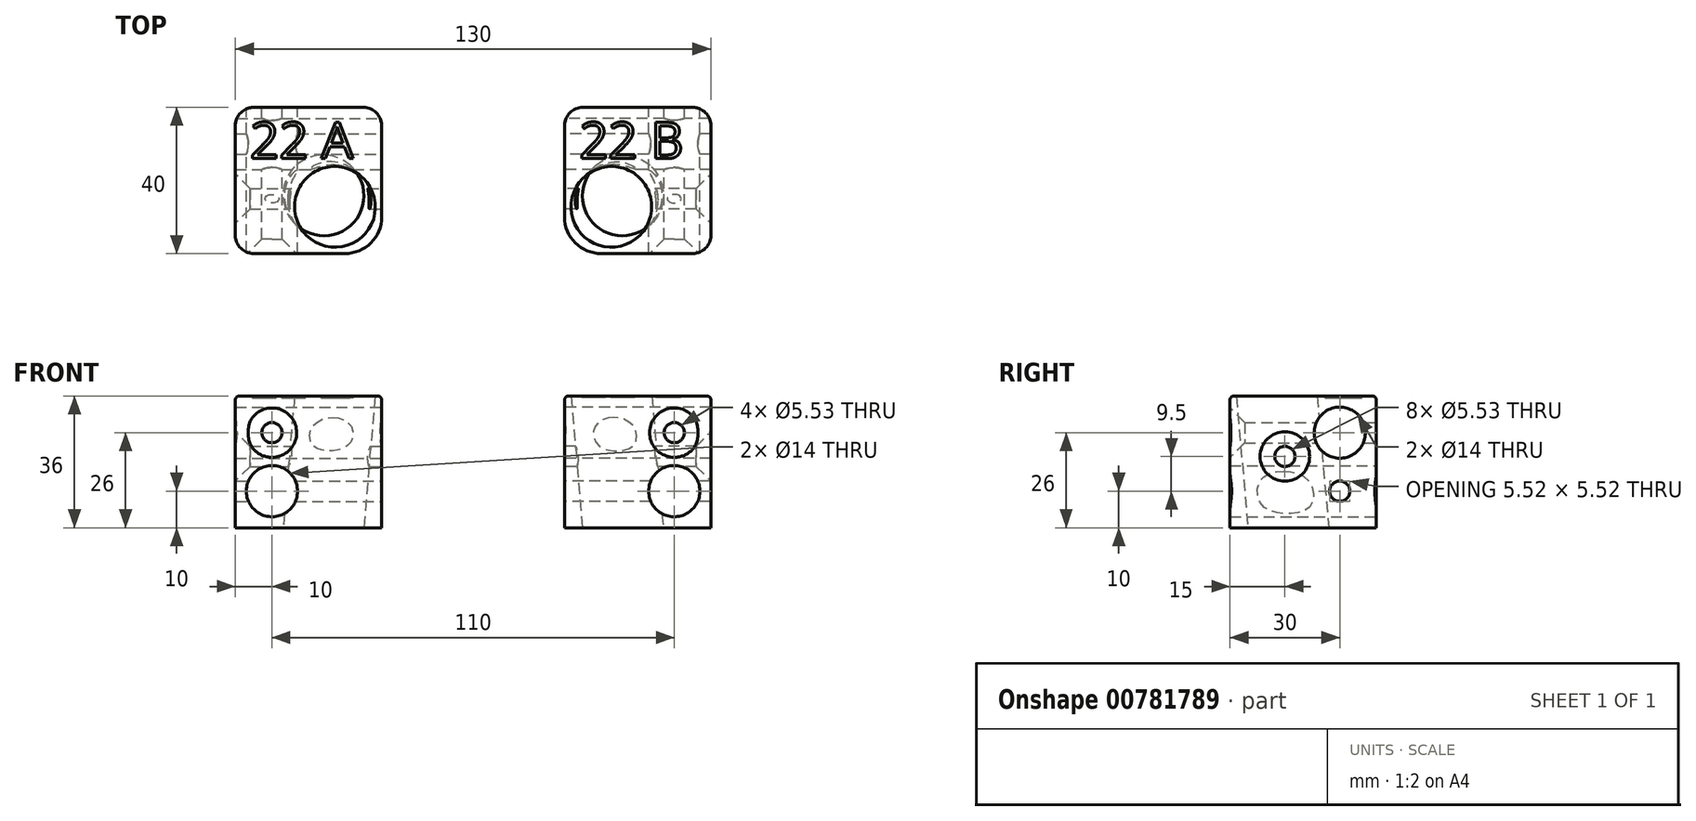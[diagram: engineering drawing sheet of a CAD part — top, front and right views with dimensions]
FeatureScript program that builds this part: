
annotation { "Feature Type Name" : "Feature", "Feature Type Description" : "" }
export const myFeature = defineFeature(function(context is Context, id is Id, definition is map)
    precondition{}
    {
        {
            var Q0;
            Q0=qCreatedBy(makeId("Right.planeOp"),FACE);
            var sketch = newSketch(context, id + "F0", { "sketchPlane" : qUnion([Q0])});
            skLineSegment(sketch, "E0", {"start": v(0, 0) * mm, "end": v(0, 73.22) * mm});
            skSolve(sketch);
        }
        {
            var Q0;
            Q0=sQuery(id+"F0.wireOp",EDGE,"E0");
            var Q1;
            Q1=qCreatedBy(makeId("Right.planeOp"),FACE);
            cPlane(context, id + "F1", {"entities" : qUnion([Q0, Q1]), "cplaneType" : CPlaneType.LINE_ANGLE, "offset" : 25 * mm, "angle" : 45 * degree, "width" : 150 * mm, "height" : 150 * mm});
        }
        {
            var Q0;
            Q0=qCreatedBy(makeId("Top.planeOp"),FACE);
            var sketch = newSketch(context, id + "F2", { "sketchPlane" : qUnion([Q0])});
            skLineSegment(sketch, "E1", {"start": v(0, 0) * mm, "end": v(6.32, 6.32) * mm});
            skSolve(sketch);
        }
        {
            var Q0;
            Q0=sQuery(id+"F2.wireOp",EDGE,"E1");
            var Q1;
            Q1=qCreatedBy(makeId("Top.planeOp"),FACE);
            cPlane(context, id + "F3", {"entities" : qUnion([Q0, Q1]), "cplaneType" : CPlaneType.LINE_ANGLE, "offset" : 25 * mm, "angle" : 7 * degree, "width" : 150 * mm, "height" : 150 * mm});
        }
        {
            var Q0;
            Q0=qCreatedBy(makeId("Top.planeOp"),FACE);
            var sketch = newSketch(context, id + "F4", { "sketchPlane" : qUnion([Q0])});
            skLineSegment(sketch, "E2.bottom", {"start": v(20, -20) * mm, "end": v(-20, -20) * mm});
            skLineSegment(sketch, "E2.top", {"start": v(20, 20) * mm, "end": v(-20, 20) * mm});
            skLineSegment(sketch, "E2.left", {"start": v(20, -20) * mm, "end": v(20, 20) * mm});
            skLineSegment(sketch, "E2.right", {"start": v(-20, -20) * mm, "end": v(-20, 20) * mm});
            skPoint(sketch, "E2.middle", {"position": v(0, 0) * mm});
            skSolve(sketch);
        }
        {
            var Q0;
            Q0=makeQuery(id+"F4.imprint","IMPRINT",FACE,{"disambiguationData":[TD([[makeQuery(id+"F4.imprint","IMPRINT",EDGE,{"derivedFrom":sQuery(id+"F4.wireOp",EDGE,"E2.bottom")}),-1.0]])]});
            extrude(context, id + "F5", {"entities" : qUnion([Q0]), "depth" : 36 * mm, "offsetDistance" : 25 * mm});
        }
        {
            var Q0;
            Q0=qCreatedBy(id+"F3.planeOp",FACE);
            var sketch = newSketch(context, id + "F6", { "sketchPlane" : qUnion([Q0])});
            skCircle(sketch, "E3", {"center": v(4.04, 4.07) * mm, "radius": 11 * mm});
            skSolve(sketch);
        }
        {
            var Q0;
            Q0 = qSketchRegion(id + "F6", true);
            extrude(context, id + "F7", {"entities" : qUnion([Q0]), "operationType" : NewBodyOperationType.REMOVE, "endBound" : BoundingType.SYMMETRIC, "oppositeDirection" : true, "depth" : 150 * mm, "offsetDistance" : 25 * mm});
        }
        {
            var Q0;
            Q0=makeQuery(id+"F5.opExtrude","SWEPT_FACE",FACE,{"disambiguationData":[OSD([sQuery(id+"F4.wireOp",EDGE,"E2.left")])]});
            var sketch = newSketch(context, id + "F8", { "sketchPlane" : qUnion([Q0])});
            skCircle(sketch, "E4", {"center": v(10, 26) * mm, "radius": 7 * mm});
            skCircle(sketch, "E5", {"center": v(10, 10) * mm, "radius": 2.76 * mm});
            skCircle(sketch, "E6", {"center": v(-5, 19.5) * mm, "radius": 2.76 * mm});
            skSolve(sketch);
        }
        {
            var Q0;
            Q0 = qSketchRegion(id + "F8", true);
            extrude(context, id + "F9", {"entities" : qUnion([Q0]), "operationType" : NewBodyOperationType.REMOVE, "endBound" : BoundingType.THROUGH_ALL, "oppositeDirection" : true, "depth" : 25 * mm, "offsetDistance" : 25 * mm});
        }
        {
            var Q0;
            Q0=makeQuery(id+"F5.opExtrude","SWEPT_FACE",FACE,{"disambiguationData":[OSD([sQuery(id+"F4.wireOp",EDGE,"E2.top")])]});
            var sketch = newSketch(context, id + "F10", { "sketchPlane" : qUnion([Q0])});
            skCircle(sketch, "E7", {"center": v(10, 10) * mm, "radius": 7 * mm});
            skCircle(sketch, "E8", {"center": v(10, 26) * mm, "radius": 2.76 * mm});
            skSolve(sketch);
        }
        {
            var Q0;
            Q0 = qSketchRegion(id + "F10", true);
            extrude(context, id + "F11", {"entities" : qUnion([Q0]), "operationType" : NewBodyOperationType.REMOVE, "endBound" : BoundingType.THROUGH_ALL, "oppositeDirection" : true, "depth" : 25 * mm, "offsetDistance" : 25 * mm});
        }
        {
            var Q0;
            Q0=makeQuery(id+"F5.opExtrude","SWEPT_EDGE",EDGE,{"disambiguationData":[OSD([sQuery(id+"F4.wireOp",EDGE,"E2.bottom"),sQuery(id+"F4.wireOp",EDGE,"E2.left")])]});
            fillet(context, id + "F12", {"entities" : qUnion([Q0]), "radius" : 10 * mm, "tangentPropagation" : true, "allowEdgeOverflow" : false});
        }
        {
            var Q0;
            Q0=makeQuery(id+"F5.opExtrude","SWEPT_EDGE",EDGE,{"disambiguationData":[OSD([sQuery(id+"F4.wireOp",EDGE,"E2.bottom"),sQuery(id+"F4.wireOp",EDGE,"E2.right")])]});
            var Q1;
            Q1=makeQuery(id+"F5.opExtrude","SWEPT_EDGE",EDGE,{"disambiguationData":[OSD([sQuery(id+"F4.wireOp",EDGE,"E2.top"),sQuery(id+"F4.wireOp",EDGE,"E2.right")])]});
            var Q2;
            Q2=makeQuery(id+"F5.opExtrude","SWEPT_EDGE",EDGE,{"disambiguationData":[OSD([sQuery(id+"F4.wireOp",EDGE,"E2.top"),sQuery(id+"F4.wireOp",EDGE,"E2.left")])]});
            fillet(context, id + "F13", {"entities" : qUnion([Q0, Q1, Q2]), "radius" : 5 * mm, "tangentPropagation" : true, "allowEdgeOverflow" : false});
        }
        {
            var Q0;
            Q0=makeQuery(id+"F5.opExtrude","CAP_EDGE",EDGE,{"disambiguationData":[OSD([sQuery(id+"F4.wireOp",EDGE,"E2.left")])],"isStart":false});
            fillet(context, id + "F14", {"entities" : qUnion([Q0]), "radius" : 1 * mm, "tangentPropagation" : true, "allowEdgeOverflow" : false});
        }
        {
            var Q0;
            Q0=makeQuery(id+"F11.boolean.opBoolean","INTERSECT",EDGE,{"derivedFrom":[makeQuery(id+"F5.opExtrude","SWEPT_FACE",FACE,{"disambiguationData":[OSD([sQuery(id+"F4.wireOp",EDGE,"E2.bottom")])]}),makeQuery(id+"F11.opExtrude","SWEPT_FACE",FACE,{"disambiguationData":[OSD([sQuery(id+"F10.wireOp",EDGE,"E8")])]})]});
            var Q1;
            Q1=makeQuery(id+"F9.boolean.opBoolean","INTERSECT",EDGE,{"derivedFrom":[makeQuery(id+"F5.opExtrude","SWEPT_FACE",FACE,{"disambiguationData":[OSD([sQuery(id+"F4.wireOp",EDGE,"E2.right")])]}),makeQuery(id+"F9.opExtrude","SWEPT_FACE",FACE,{"disambiguationData":[OSD([sQuery(id+"F8.wireOp",EDGE,"E6")])]})]});
            var Q2;
            Q2=makeQuery(id+"F9.boolean.opBoolean","COPY",EDGE,{"derivedFrom":makeQuery(id+"F9.opExtrude","CAP_EDGE",EDGE,{"disambiguationData":[OSD([sQuery(id+"F8.wireOp",EDGE,"E5")])],"isStart":true})});
            chamfer(context, id + "F15", {"entities" : qUnion([Q0, Q1, Q2]), "width" : 4 * mm, "tangentPropagation" : true});
        }
        {
            var Q0;
            Q0=makeQuery(id+"F5.opExtrude","SWEPT_FACE",FACE,{"disambiguationData":[OSD([sQuery(id+"F4.wireOp",EDGE,"E2.left")])]});
            cPlane(context, id + "F16", {"entities" : qUnion([Q0]), "cplaneType" : CPlaneType.OFFSET, "offset" : 25 * mm, "width" : 150 * mm, "height" : 150 * mm});
        }
        {
            var Q0;
            Q0=makeQuery(id+"F5.opExtrude","SWEPT_BODY",BODY,{"disambiguationData":[OSD([sQuery(id+"F4.wireOp",EDGE,"E2.bottom"),sQuery(id+"F4.wireOp",EDGE,"E2.top"),sQuery(id+"F4.wireOp",EDGE,"E2.left"),sQuery(id+"F4.wireOp",EDGE,"E2.right")])]});
            var Q1;
            Q1=qCreatedBy(id+"F16.planeOp",FACE);
            mirror(context, id + "F17", {"entities" : qUnion([Q0]), "mirrorPlane" : qUnion([Q1])});
        }
        {
            var Q0;
            Q0=makeQuery(id+"F5.opExtrude","CAP_FACE",FACE,{"disambiguationData":[OSD([sQuery(id+"F4.wireOp",EDGE,"E2.bottom"),sQuery(id+"F4.wireOp",EDGE,"E2.top"),sQuery(id+"F4.wireOp",EDGE,"E2.left"),sQuery(id+"F4.wireOp",EDGE,"E2.right")])],"isStart":false});
            var sketch = newSketch(context, id + "F18", { "sketchPlane" : qUnion([Q0])});
            skText(sketch, "E9", { "text": "18", "fontName": "OpenSans-Regular.ttf"});
            const initialGuessF18  = {"E9": [-0.00694, 0.0067, 1, 0, 0.00963]};
            skSetInitialGuess(sketch, initialGuessF18);
            skSolve(sketch);
        }
        {
            var Q0;
            Q0=makeQuery(id+"F5.opExtrude","CAP_FACE",FACE,{"disambiguationData":[OSD([sQuery(id+"F4.wireOp",EDGE,"E2.bottom"),sQuery(id+"F4.wireOp",EDGE,"E2.top"),sQuery(id+"F4.wireOp",EDGE,"E2.left"),sQuery(id+"F4.wireOp",EDGE,"E2.right")])],"isStart":false});
            var sketch = newSketch(context, id + "F19", { "sketchPlane" : qUnion([Q0])});
            skText(sketch, "E10", { "text": "22 A", "fontName": "OpenSans-Regular.ttf"});
            const initialGuessF19  = {"E10": [-0.016, 0.006, 1, 0, 0.01]};
            skSetInitialGuess(sketch, initialGuessF19);
            skSolve(sketch);
        }
        {
            var Q0;
            Q0 = qSketchRegion(id + "F19", true);
            extrude(context, id + "F20", {"entities" : qUnion([Q0]), "operationType" : NewBodyOperationType.REMOVE, "oppositeDirection" : true, "depth" : .5 * mm, "offsetDistance" : 25 * mm});
        }
        {
            var Q0;
            Q0=makeQuery(id+"F17.opPattern","COPY",FACE,{"derivedFrom":makeQuery(id+"F5.opExtrude","CAP_FACE",FACE,{"disambiguationData":[OSD([sQuery(id+"F4.wireOp",EDGE,"E2.bottom"),sQuery(id+"F4.wireOp",EDGE,"E2.top"),sQuery(id+"F4.wireOp",EDGE,"E2.left"),sQuery(id+"F4.wireOp",EDGE,"E2.right")])],"isStart":false}),"instanceName":"1"});
            var sketch = newSketch(context, id + "F21", { "sketchPlane" : qUnion([Q0])});
            skText(sketch, "E11", { "text": "22 B", "fontName": "OpenSans-Regular.ttf"});
            const initialGuessF21  = {"E11": [0.074, 0.006, 1, 0, 0.01]};
            skSetInitialGuess(sketch, initialGuessF21);
            skSolve(sketch);
        }
        {
            var Q0;
            Q0 = qSketchRegion(id + "F21", true);
            extrude(context, id + "F22", {"entities" : qUnion([Q0]), "operationType" : NewBodyOperationType.REMOVE, "oppositeDirection" : true, "depth" : .3 * mm, "offsetDistance" : 25 * mm});
        }
    });
